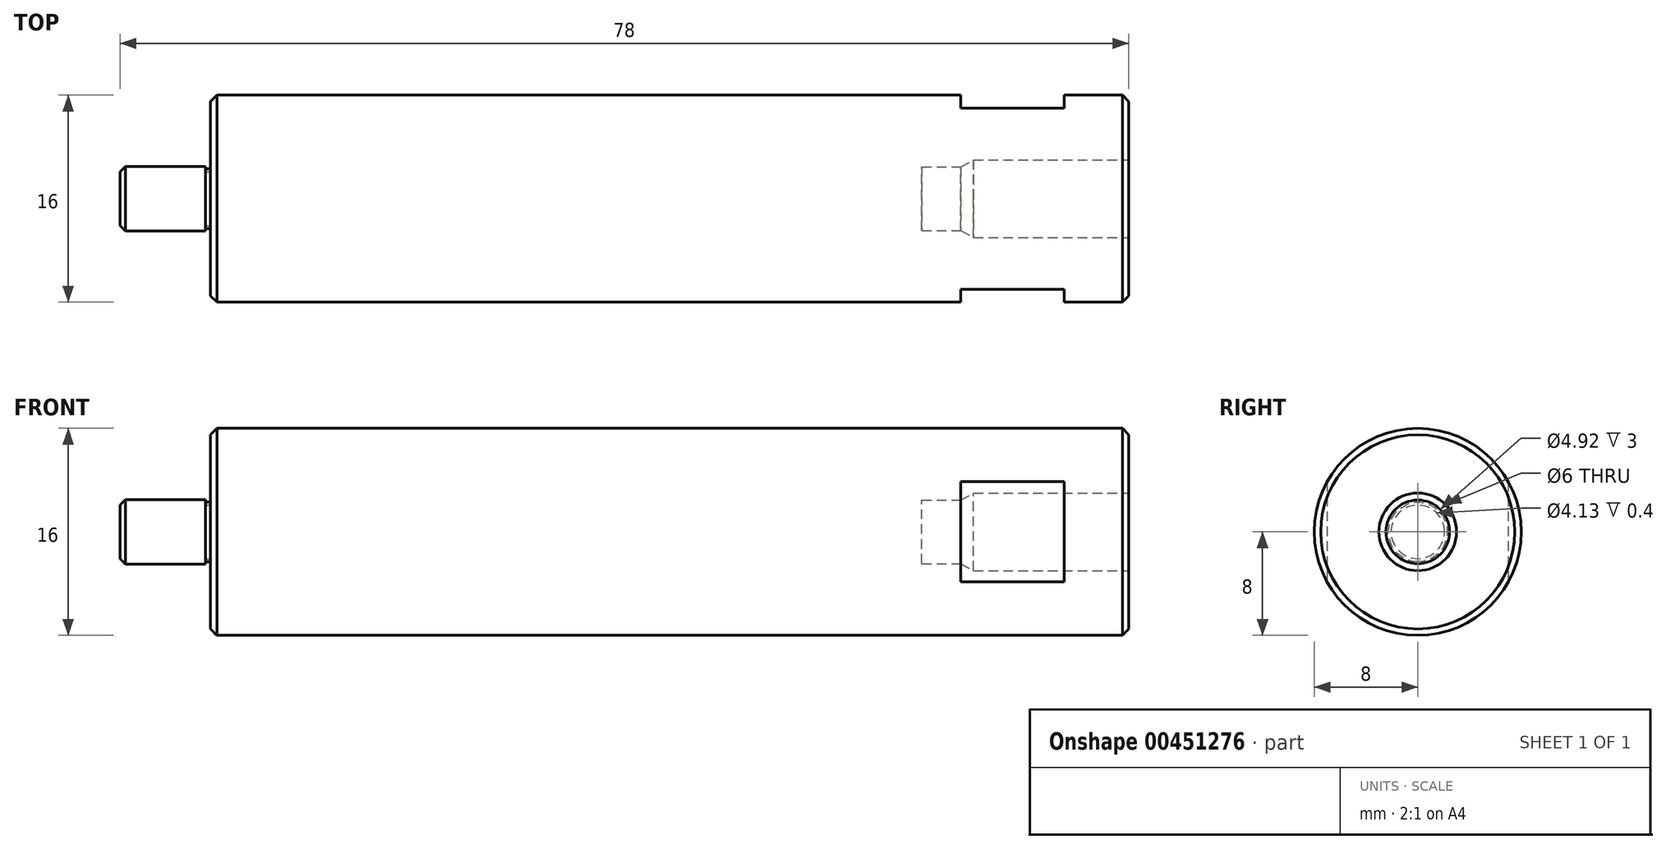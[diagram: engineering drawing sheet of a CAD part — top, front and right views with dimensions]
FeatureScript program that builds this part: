
annotation { "Feature Type Name" : "Feature", "Feature Type Description" : "" }
export const myFeature = defineFeature(function(context is Context, id is Id, definition is map)
    precondition{}
    {
        {
            var Q0;
            Q0=qCreatedBy(makeId("Front.planeOp"),FACE);
            var sketch = newSketch(context, id + "F0", { "sketchPlane" : qUnion([Q0])});
            skCircle(sketch, "E0", {"center": v(27.38, -91.67) * mm, "radius": 8 * mm});
            skLineSegment(sketch, "E1", {"start": v(20.38, -95.54) * mm, "end": v(20.38, -87.8) * mm});
            skLineSegment(sketch, "E2", {"start": v(34.38, -95.54) * mm, "end": v(34.38, -87.8) * mm});
            skLineSegment(sketch, "E3", {"start": v(27.38, -102.07) * mm, "end": v(27.38, -81.27) * mm});
            skLineSegment(sketch, "E4", {"start": v(37.78, -91.67) * mm, "end": v(16.98, -91.67) * mm});
            skLineSegment(sketch, "E5", {"start": v(-10.5, -91.67) * mm, "end": v(-105.05, -91.67) * mm});
            skLineSegment(sketch, "E6", {"start": v(-91.24, -99.17) * mm, "end": v(-91.24, -84.17) * mm});
            skLineSegment(sketch, "E7", {"start": v(-20.24, -84.17) * mm, "end": v(-20.24, -99.17) * mm});
            skLineSegment(sketch, "E8", {"start": v(-20.74, -99.67) * mm, "end": v(-90.74, -99.67) * mm});
            skLineSegment(sketch, "E9", {"start": v(-20.74, -83.67) * mm, "end": v(-90.74, -83.67) * mm});
            skLineSegment(sketch, "E10", {"start": v(-98.24, -89.6) * mm, "end": v(-98.24, -93.74) * mm});
            skLineSegment(sketch, "E11", {"start": v(-91.24, -89.6) * mm, "end": v(-98.24, -89.6) * mm});
            skLineSegment(sketch, "E12", {"start": v(-91.24, -93.74) * mm, "end": v(-98.24, -93.74) * mm});
            skLineSegment(sketch, "E13", {"start": v(-91.64, -89.17) * mm, "end": v(-97.8, -89.17) * mm});
            skLineSegment(sketch, "E14", {"start": v(-91.64, -94.17) * mm, "end": v(-97.8, -94.17) * mm});
            skLineSegment(sketch, "E15", {"start": v(-91.24, -87.05) * mm, "end": v(-91.24, -96.29) * mm});
            skLineSegment(sketch, "E16", {"start": v(-98.24, -93.74) * mm, "end": v(-97.8, -94.17) * mm});
            skLineSegment(sketch, "E17", {"start": v(-98.24, -89.6) * mm, "end": v(-97.8, -89.17) * mm});
            skLineSegment(sketch, "E18", {"start": v(-97.8, -94.17) * mm, "end": v(-97.8, -89.17) * mm});
            skLineSegment(sketch, "E19", {"start": v(-32.24, -94.67) * mm, "end": v(-32.24, -88.67) * mm});
            skLineSegment(sketch, "E20", {"start": v(-32.24, -88.67) * mm, "end": v(-33.24, -89.21) * mm});
            skLineSegment(sketch, "E21", {"start": v(-20.24, -88.67) * mm, "end": v(-32.24, -88.67) * mm});
            skLineSegment(sketch, "E22", {"start": v(-37.66, -91.67) * mm, "end": v(-20.24, -91.67) * mm});
            skLineSegment(sketch, "E23", {"start": v(-20.24, -89.21) * mm, "end": v(-36.24, -89.21) * mm});
            skLineSegment(sketch, "E24", {"start": v(-20.24, -94.67) * mm, "end": v(-32.24, -94.67) * mm});
            skLineSegment(sketch, "E25", {"start": v(-20.24, -94.13) * mm, "end": v(-36.24, -94.13) * mm});
            skLineSegment(sketch, "E26", {"start": v(-37.66, -91.67) * mm, "end": v(-36.24, -89.21) * mm});
            skLineSegment(sketch, "E27", {"start": v(-36.24, -94.13) * mm, "end": v(-36.24, -89.21) * mm});
            skLineSegment(sketch, "E28", {"start": v(-37.66, -91.67) * mm, "end": v(-36.24, -94.13) * mm});
            skLineSegment(sketch, "E29", {"start": v(-32.24, -94.67) * mm, "end": v(-33.24, -94.13) * mm});
            skLineSegment(sketch, "E30", {"start": v(-25.24, -87.8) * mm, "end": v(-25.24, -95.54) * mm});
            skLineSegment(sketch, "E31", {"start": v(-33.24, -87.8) * mm, "end": v(-33.24, -95.54) * mm});
            skLineSegment(sketch, "E32", {"start": v(-25.24, -87.8) * mm, "end": v(-33.24, -87.8) * mm});
            skLineSegment(sketch, "E33", {"start": v(-25.24, -95.54) * mm, "end": v(-33.24, -95.54) * mm});
            skLineSegment(sketch, "E34", {"start": v(-25.24, -87.8) * mm, "end": v(-33.24, -95.54) * mm});
            skLineSegment(sketch, "E35", {"start": v(-25.24, -95.54) * mm, "end": v(-33.24, -87.8) * mm});
            skLineSegment(sketch, "E36", {"start": v(31.88, -91.67) * mm, "end": v(22.88, -91.67) * mm});
            skCircle(sketch, "E37", {"center": v(27.38, -91.67) * mm, "radius": 3 * mm});
            skLineSegment(sketch, "E38", {"start": v(27.38, -96.17) * mm, "end": v(27.38, -87.17) * mm});
            skCircle(sketch, "E39", {"center": v(27.38, -91.67) * mm, "radius": 2.46 * mm});
            skLineSegment(sketch, "E40", {"start": v(-20.24, -84.17) * mm, "end": v(-20.74, -83.67) * mm});
            skLineSegment(sketch, "E41", {"start": v(-20.24, -99.17) * mm, "end": v(-20.74, -99.67) * mm});
            skLineSegment(sketch, "E42", {"start": v(-20.74, -99.67) * mm, "end": v(-20.74, -83.67) * mm});
            skLineSegment(sketch, "E43", {"start": v(-90.74, -99.67) * mm, "end": v(-91.24, -99.17) * mm});
            skLineSegment(sketch, "E44", {"start": v(-90.74, -83.67) * mm, "end": v(-91.24, -84.17) * mm});
            skLineSegment(sketch, "E45", {"start": v(-90.74, -99.67) * mm, "end": v(-90.74, -83.67) * mm});
            skLineSegment(sketch, "E46", {"start": v(-91.64, -89.17) * mm, "end": v(-91.64, -94.17) * mm});
            skArc(sketch, "E47", {"start": v(-91.64, -89.17) * mm, "mid": v(-91.44, -89.37) * mm, "end": v(-91.24, -89.17) * mm});
            skArc(sketch, "E48", {"start": v(-91.24, -94.17) * mm, "mid": v(-91.44, -93.97) * mm, "end": v(-91.64, -94.17) * mm});
            skSolve(sketch);
        }
        {
            var Q0;
            {var subQ10=sQuery(id+"F0.wireOp",EDGE,"E9");Q0=makeQuery(id+"F0.imprint","IMPRINT",FACE,{"disambiguationData":[TD([[makeQuery(id+"F0.imprint","IMPRINT",EDGE,{"derivedFrom":subQ10}),1.0]])]});}
            var Q1;
            {var subQ0=sQuery(id+"F0.wireOp",EDGE,"E30");var subQ1=sQuery(id+"F0.wireOp",EDGE,"E21");var subQ2=makeQuery(id+"F0.imprint","INTERSECT",VERTEX,{"derivedFrom":[subQ1,subQ0]});Q1=makeQuery(id+"F0.imprint","IMPRINT",FACE,{"disambiguationData":[TD([[makeQuery(id+"F0.imprint","IMPRINT",EDGE,{"disambiguationData":[TD([[subQ2,-1.0]])],"derivedFrom":subQ1}),-1.0]])]});}
            var Q2;
            {var subQ1=sQuery(id+"F0.wireOp",EDGE,"E32");Q2=makeQuery(id+"F0.imprint","IMPRINT",FACE,{"disambiguationData":[TD([[makeQuery(id+"F0.imprint","IMPRINT",EDGE,{"derivedFrom":subQ1}),1.0]])]});}
            var Q3;
            {var subQ1=sQuery(id+"F0.wireOp",EDGE,"E20");var subQ3=sQuery(id+"F0.wireOp",EDGE,"E35");var subQ4=makeQuery(id+"F0.imprint","INTERSECT",VERTEX,{"derivedFrom":[subQ1,subQ3]});Q3=makeQuery(id+"F0.imprint","IMPRINT",FACE,{"disambiguationData":[TD([[makeQuery(id+"F0.imprint","IMPRINT",EDGE,{"disambiguationData":[TD([[subQ4,-1.0]])],"derivedFrom":subQ1}),-1.0]])]});}
            var Q4;
            {var subQ0=sQuery(id+"F0.wireOp",EDGE,"E40");Q4=makeQuery(id+"F0.imprint","IMPRINT",FACE,{"disambiguationData":[TD([[makeQuery(id+"F0.imprint","IMPRINT",EDGE,{"derivedFrom":subQ0}),1.0]])]});}
            var Q5;
            {var subQ4=sQuery(id+"F0.wireOp",EDGE,"E44");Q5=makeQuery(id+"F0.imprint","IMPRINT",FACE,{"disambiguationData":[TD([[makeQuery(id+"F0.imprint","IMPRINT",EDGE,{"derivedFrom":subQ4}),1.0]])]});}
            var Q6;
            {var subQ0=sQuery(id+"F0.wireOp",EDGE,"E15");var subQ1=sQuery(id+"F0.wireOp",EDGE,"E5");var subQ2=makeQuery(id+"F0.imprint","INTERSECT",VERTEX,{"derivedFrom":[subQ1,subQ0]});Q6=makeQuery(id+"F0.imprint","IMPRINT",FACE,{"disambiguationData":[TD([[makeQuery(id+"F0.imprint","IMPRINT",EDGE,{"disambiguationData":[TD([[subQ2,-1.0]])],"derivedFrom":subQ1}),-1.0]])]});}
            var Q7;
            {var subQ5=sQuery(id+"F0.wireOp",EDGE,"E47");Q7=makeQuery(id+"F0.imprint","IMPRINT",FACE,{"disambiguationData":[TD([[makeQuery(id+"F0.imprint","IMPRINT",EDGE,{"derivedFrom":subQ5}),-1.0]])]});}
            var Q8;
            {var subQ5=sQuery(id+"F0.wireOp",EDGE,"E13");Q8=makeQuery(id+"F0.imprint","IMPRINT",FACE,{"disambiguationData":[TD([[makeQuery(id+"F0.imprint","IMPRINT",EDGE,{"derivedFrom":subQ5}),1.0]])]});}
            var Q9;
            {var subQ0=sQuery(id+"F0.wireOp",EDGE,"E46");var subQ1=sQuery(id+"F0.wireOp",EDGE,"E5");var subQ2=makeQuery(id+"F0.imprint","INTERSECT",VERTEX,{"derivedFrom":[subQ1,subQ0]});Q9=makeQuery(id+"F0.imprint","IMPRINT",FACE,{"disambiguationData":[TD([[makeQuery(id+"F0.imprint","IMPRINT",EDGE,{"disambiguationData":[TD([[subQ2,-1.0]])],"derivedFrom":subQ1}),-1.0]])]});}
            var Q10;
            {var subQ0=sQuery(id+"F0.wireOp",EDGE,"E10");var subQ1=sQuery(id+"F0.wireOp",EDGE,"E5");var subQ2=makeQuery(id+"F0.imprint","INTERSECT",VERTEX,{"derivedFrom":[subQ1,subQ0]});Q10=makeQuery(id+"F0.imprint","IMPRINT",FACE,{"disambiguationData":[TD([[makeQuery(id+"F0.imprint","IMPRINT",EDGE,{"disambiguationData":[TD([[subQ2,1.0]])],"derivedFrom":subQ1}),-1.0]])]});}
            var Q11;
            {var subQ0=sQuery(id+"F0.wireOp",EDGE,"E17");Q11=makeQuery(id+"F0.imprint","IMPRINT",FACE,{"disambiguationData":[TD([[makeQuery(id+"F0.imprint","IMPRINT",EDGE,{"derivedFrom":subQ0}),-1.0]])]});}
            var Q12;
            Q12=sQuery(id+"F0.wireOp",EDGE,"E5");
            revolve(context, id + "F1", {"entities" : qUnion([Q0, Q1, Q2, Q3, Q4, Q5, Q6, Q7, Q8, Q9, Q10, Q11]), "axis" : qUnion([Q12]), "revolveType" : RevolveType.FULL});
        }
        {
            var Q0;
            Q0=makeQuery(id+"F1.opRevolve","SWEPT_FACE",FACE,{"disambiguationData":[OSD([sQuery(id+"F0.wireOp",EDGE,"E7")])]});
            cPlane(context, id + "F2", {"entities" : qUnion([Q0]), "cplaneType" : CPlaneType.OFFSET, "offset" : 13 * mm, "oppositeDirection" : true, "width" : 150 * mm, "height" : 150 * mm});
        }
        {
            var Q0;
            Q0=qCreatedBy(id+"F2.planeOp",FACE);
            var sketch = newSketch(context, id + "F3", { "sketchPlane" : qUnion([Q0])});
            skLineSegment(sketch, "E49", {"start": v(0, -81.29) * mm, "end": v(0, -105.1) * mm});
            skLineSegment(sketch, "E50.0", {"start": v(-7, -81.29) * mm, "end": v(-7, -105.1) * mm});
            skLineSegment(sketch, "E51.0", {"start": v(7, -81.29) * mm, "end": v(7, -105.1) * mm});
            skLineSegment(sketch, "E52", {"start": v(7, -81.29) * mm, "end": v(14.3, -81.29) * mm});
            skLineSegment(sketch, "E53", {"start": v(14.3, -81.29) * mm, "end": v(14.3, -107.92) * mm});
            skLineSegment(sketch, "E54", {"start": v(14.3, -107.92) * mm, "end": v(7, -105.1) * mm});
            skLineSegment(sketch, "E55", {"start": v(-7, -105.1) * mm, "end": v(-15.8, -106.5) * mm});
            skLineSegment(sketch, "E56", {"start": v(-15.8, -106.5) * mm, "end": v(-14.85, -81.29) * mm});
            skLineSegment(sketch, "E57", {"start": v(-14.85, -81.29) * mm, "end": v(-7, -81.29) * mm});
            skSolve(sketch);
        }
        {
            var Q0;
            Q0 = qSketchRegion(id + "F3", true);
            extrude(context, id + "F4", {"entities" : qUnion([Q0]), "operationType" : NewBodyOperationType.REMOVE, "depth" : 8 * mm});
        }
    });
